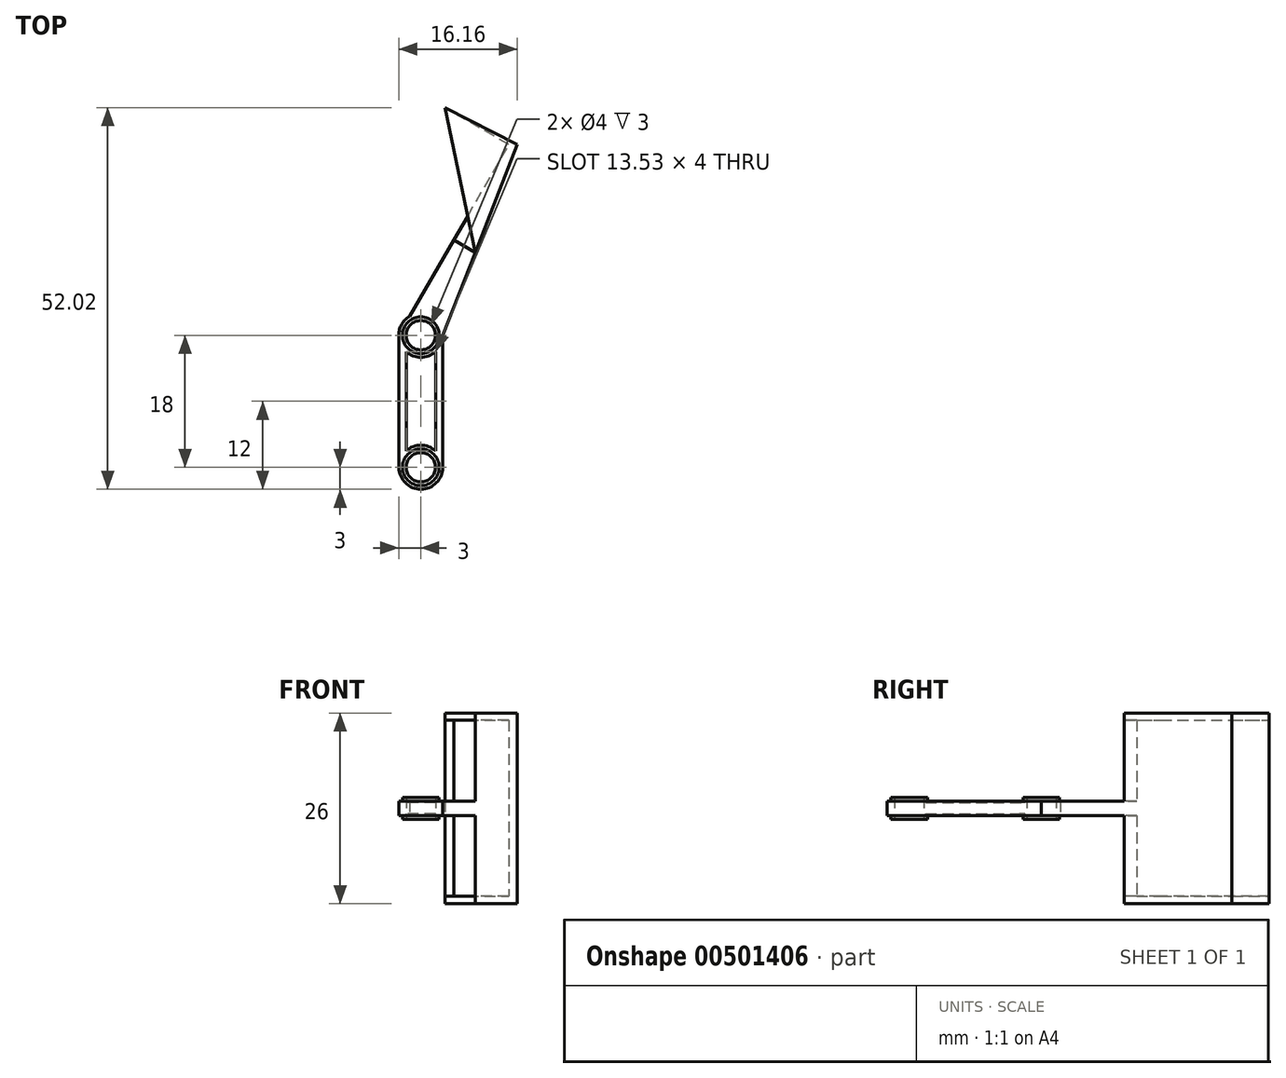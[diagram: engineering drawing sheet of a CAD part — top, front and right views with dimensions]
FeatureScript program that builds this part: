
annotation { "Feature Type Name" : "Feature", "Feature Type Description" : "" }
export const myFeature = defineFeature(function(context is Context, id is Id, definition is map)
    precondition{}
    {
        {
            var Q0;
            Q0=qCreatedBy(makeId("Front.planeOp"),FACE);
            var sketch = newSketch(context, id + "F0", { "sketchPlane" : qUnion([Q0])});
            skLineSegment(sketch, "E0.left", {"start": v(3, -1) * mm, "end": v(3, 1) * mm});
            skLineSegment(sketch, "E0.right", {"start": v(-3, -1) * mm, "end": v(-3, 1) * mm});
            skPoint(sketch, "E0.middle", {"position": v(0, 0) * mm});
            skLineSegment(sketch, "E1", {"start": v(-3, 1) * mm, "end": v(-2, 1) * mm});
            skLineSegment(sketch, "E2", {"start": v(-2, 1) * mm, "end": v(-2, 0.75) * mm});
            skLineSegment(sketch, "E3", {"start": v(-2, 0.75) * mm, "end": v(2, 0.75) * mm});
            skLineSegment(sketch, "E4", {"start": v(2, 0.75) * mm, "end": v(2, 1) * mm});
            skLineSegment(sketch, "E5", {"start": v(2, 1) * mm, "end": v(3, 1) * mm});
            skLineSegment(sketch, "E6", {"start": v(-3, -1) * mm, "end": v(-2, -1) * mm});
            skLineSegment(sketch, "E7", {"start": v(-2, -1) * mm, "end": v(-2, -0.75) * mm});
            skLineSegment(sketch, "E8", {"start": v(-2, -0.75) * mm, "end": v(2, -0.75) * mm});
            skLineSegment(sketch, "E9", {"start": v(2, -0.75) * mm, "end": v(2, -1) * mm});
            skLineSegment(sketch, "E10", {"start": v(2, -1) * mm, "end": v(3, -1) * mm});
            skSolve(sketch);
        }
        {
            var Q0;
            Q0=makeQuery(id+"F0.imprint","IMPRINT",FACE,{"disambiguationData":[TD([[makeQuery(id+"F0.imprint","IMPRINT",EDGE,{"derivedFrom":sQuery(id+"F0.wireOp",EDGE,"E0.left")}),1.0]])]});
            extrude(context, id + "F1", {"entities" : qUnion([Q0]), "endBound" : BoundingType.SYMMETRIC, "depth" : 18 * mm});
        }
        {
            var Q0;
            Q0=makeQuery(id+"F1.opExtrude","SWEPT_FACE",FACE,{"disambiguationData":[OSD([sQuery(id+"F0.wireOp",EDGE,"E8")])]});
            var sketch = newSketch(context, id + "F2", { "sketchPlane" : qUnion([Q0])});
            skCircle(sketch, "E11", {"center": v(0, 9) * mm, "radius": 2 * mm});
            skCircle(sketch, "E12", {"center": v(0, 9) * mm, "radius": 3 * mm});
            skCircle(sketch, "E13", {"center": v(0, -9) * mm, "radius": 2 * mm});
            skPoint(sketch, "E13.centerSnap0", {"position": v(0, -9) * mm});
            skCircle(sketch, "E14", {"center": v(0, -9) * mm, "radius": 3 * mm});
            skSolve(sketch);
        }
        {
            var Q0;
            {var subQ1=sQuery(id+"F0.wireOp",EDGE,"E8");var subQ2=makeQuery(id+"F1.opExtrude","CAP_EDGE",EDGE,{"disambiguationData":[OSD([subQ1])],"isStart":false});Q0=makeQuery(id+"F2.imprint","IMPRINT",FACE,{"disambiguationData":[TD([[makeQuery(id+"F2.imprint","IMPRINT",EDGE,{"derivedFrom":subQ2}),-1.0]])]});}
            extrude(context, id + "F3", {"entities" : qUnion([Q0]), "operationType" : NewBodyOperationType.REMOVE, "oppositeDirection" : true, "depth" : 2 * mm});
        }
        {
            var Q0;
            {var subQ1=sQuery(id+"F0.wireOp",EDGE,"E8");var subQ2=makeQuery(id+"F1.opExtrude","CAP_EDGE",EDGE,{"disambiguationData":[OSD([subQ1])],"isStart":true});Q0=makeQuery(id+"F2.imprint","IMPRINT",FACE,{"disambiguationData":[TD([[makeQuery(id+"F2.imprint","IMPRINT",EDGE,{"derivedFrom":subQ2}),1.0]])]});}
            extrude(context, id + "F4", {"entities" : qUnion([Q0]), "operationType" : NewBodyOperationType.REMOVE, "oppositeDirection" : true, "depth" : 2 * mm});
        }
        {
            var Q0;
            {var subQ1=sQuery(id+"F0.wireOp",EDGE,"E8");var subQ3=makeQuery(id+"F1.opExtrude","SWEPT_EDGE",EDGE,{"disambiguationData":[OSD([sQuery(id+"F0.wireOp",EDGE,"E7"),subQ1])]});var subQ7=sQuery(id+"F2.wireOp",EDGE,"E14");var subQ8=makeQuery(id+"F2.imprint","INTERSECT",VERTEX,{"derivedFrom":[subQ3,subQ7]});Q0=makeQuery(id+"F2.imprint","IMPRINT",FACE,{"disambiguationData":[TD([[makeQuery(id+"F2.imprint","IMPRINT",EDGE,{"disambiguationData":[TD([[subQ8,-1.0]])],"derivedFrom":subQ7}),1.0]])]});}
            var Q1;
            {var subQ1=sQuery(id+"F0.wireOp",EDGE,"E8");var subQ3=makeQuery(id+"F1.opExtrude","SWEPT_EDGE",EDGE,{"disambiguationData":[OSD([sQuery(id+"F0.wireOp",EDGE,"E7"),subQ1])]});var subQ7=sQuery(id+"F2.wireOp",EDGE,"E14");var subQ8=makeQuery(id+"F2.imprint","INTERSECT",VERTEX,{"derivedFrom":[subQ3,subQ7]});Q1=makeQuery(id+"F2.imprint","IMPRINT",FACE,{"disambiguationData":[TD([[makeQuery(id+"F2.imprint","IMPRINT",EDGE,{"disambiguationData":[TD([[subQ8,1.0]])],"derivedFrom":subQ7}),1.0]])]});}
            extrude(context, id + "F5", {"entities" : qUnion([Q0, Q1]), "operationType" : NewBodyOperationType.REMOVE, "oppositeDirection" : true, "depth" : 2 * mm});
        }
        {
            var Q0;
            {var subQ1=sQuery(id+"F0.wireOp",EDGE,"E8");var subQ3=makeQuery(id+"F1.opExtrude","SWEPT_EDGE",EDGE,{"disambiguationData":[OSD([sQuery(id+"F0.wireOp",EDGE,"E7"),subQ1])]});var subQ7=sQuery(id+"F2.wireOp",EDGE,"E14");var subQ8=makeQuery(id+"F2.imprint","INTERSECT",VERTEX,{"derivedFrom":[subQ3,subQ7]});Q0=makeQuery(id+"F2.imprint","IMPRINT",FACE,{"disambiguationData":[TD([[makeQuery(id+"F2.imprint","IMPRINT",EDGE,{"disambiguationData":[TD([[subQ8,-1.0]])],"derivedFrom":subQ7}),1.0]])]});}
            extrude(context, id + "F6", {"entities" : qUnion([Q0]), "operationType" : NewBodyOperationType.REMOVE, "oppositeDirection" : true, "depth" : 25 * mm});
        }
        {
            var Q0;
            {var subQ1=sQuery(id+"F0.wireOp",EDGE,"E8");var subQ3=makeQuery(id+"F1.opExtrude","SWEPT_EDGE",EDGE,{"disambiguationData":[OSD([sQuery(id+"F0.wireOp",EDGE,"E7"),subQ1])]});var subQ7=sQuery(id+"F2.wireOp",EDGE,"E14");var subQ8=makeQuery(id+"F2.imprint","INTERSECT",VERTEX,{"derivedFrom":[subQ3,subQ7]});Q0=makeQuery(id+"F2.imprint","IMPRINT",FACE,{"disambiguationData":[TD([[makeQuery(id+"F2.imprint","IMPRINT",EDGE,{"disambiguationData":[TD([[subQ8,-1.0]])],"derivedFrom":subQ7}),1.0]])]});}
            extrude(context, id + "F7", {"entities" : qUnion([Q0]), "operationType" : NewBodyOperationType.REMOVE, "oppositeDirection" : true, "depth" : 25 * mm});
        }
        {
            var Q0;
            {var subQ1=sQuery(id+"F0.wireOp",EDGE,"E8");var subQ3=makeQuery(id+"F1.opExtrude","SWEPT_EDGE",EDGE,{"disambiguationData":[OSD([sQuery(id+"F0.wireOp",EDGE,"E7"),subQ1])]});var subQ7=sQuery(id+"F2.wireOp",EDGE,"E14");var subQ8=makeQuery(id+"F2.imprint","INTERSECT",VERTEX,{"derivedFrom":[subQ3,subQ7]});Q0=makeQuery(id+"F2.imprint","IMPRINT",FACE,{"disambiguationData":[TD([[makeQuery(id+"F2.imprint","IMPRINT",EDGE,{"disambiguationData":[TD([[subQ8,-1.0]])],"derivedFrom":subQ7}),1.0]])]});}
            extrude(context, id + "F8", {"entities" : qUnion([Q0]), "operationType" : NewBodyOperationType.REMOVE, "oppositeDirection" : true, "depth" : 25 * mm});
        }
        {
            var Q0;
            {var subQ1=sQuery(id+"F0.wireOp",EDGE,"E8");var subQ3=makeQuery(id+"F1.opExtrude","SWEPT_EDGE",EDGE,{"disambiguationData":[OSD([sQuery(id+"F0.wireOp",EDGE,"E7"),subQ1])]});var subQ7=sQuery(id+"F2.wireOp",EDGE,"E14");var subQ8=makeQuery(id+"F2.imprint","INTERSECT",VERTEX,{"derivedFrom":[subQ3,subQ7]});Q0=makeQuery(id+"F2.imprint","IMPRINT",FACE,{"disambiguationData":[TD([[makeQuery(id+"F2.imprint","IMPRINT",EDGE,{"disambiguationData":[TD([[subQ8,-1.0]])],"derivedFrom":subQ7}),1.0]])]});}
            extrude(context, id + "F9", {"entities" : qUnion([Q0]), "operationType" : NewBodyOperationType.REMOVE, "depth" : 2 * mm});
        }
        {
            var Q0;
            {var subQ1=sQuery(id+"F0.wireOp",EDGE,"E8");var subQ3=makeQuery(id+"F1.opExtrude","SWEPT_EDGE",EDGE,{"disambiguationData":[OSD([sQuery(id+"F0.wireOp",EDGE,"E7"),subQ1])]});var subQ7=sQuery(id+"F2.wireOp",EDGE,"E12");var subQ8=makeQuery(id+"F2.imprint","INTERSECT",VERTEX,{"derivedFrom":[subQ3,subQ7]});Q0=makeQuery(id+"F2.imprint","IMPRINT",FACE,{"disambiguationData":[TD([[makeQuery(id+"F2.imprint","IMPRINT",EDGE,{"disambiguationData":[TD([[subQ8,1.0]])],"derivedFrom":subQ7}),1.0]])]});}
            var Q1;
            {var subQ1=sQuery(id+"F0.wireOp",EDGE,"E8");var subQ3=makeQuery(id+"F1.opExtrude","SWEPT_EDGE",EDGE,{"disambiguationData":[OSD([sQuery(id+"F0.wireOp",EDGE,"E7"),subQ1])]});var subQ7=sQuery(id+"F2.wireOp",EDGE,"E12");var subQ8=makeQuery(id+"F2.imprint","INTERSECT",VERTEX,{"derivedFrom":[subQ3,subQ7]});Q1=makeQuery(id+"F2.imprint","IMPRINT",FACE,{"disambiguationData":[TD([[makeQuery(id+"F2.imprint","IMPRINT",EDGE,{"disambiguationData":[TD([[subQ8,-1.0]])],"derivedFrom":subQ7}),1.0]])]});}
            extrude(context, id + "F10", {"entities" : qUnion([Q0, Q1]), "operationType" : NewBodyOperationType.REMOVE, "oppositeDirection" : true, "depth" : 2 * mm});
        }
        {
            var Q0;
            {var subQ1=sQuery(id+"F0.wireOp",EDGE,"E8");var subQ3=makeQuery(id+"F1.opExtrude","SWEPT_EDGE",EDGE,{"disambiguationData":[OSD([sQuery(id+"F0.wireOp",EDGE,"E7"),subQ1])]});var subQ7=sQuery(id+"F2.wireOp",EDGE,"E12");var subQ8=makeQuery(id+"F2.imprint","INTERSECT",VERTEX,{"derivedFrom":[subQ3,subQ7]});Q0=makeQuery(id+"F2.imprint","IMPRINT",FACE,{"disambiguationData":[TD([[makeQuery(id+"F2.imprint","IMPRINT",EDGE,{"disambiguationData":[TD([[subQ8,1.0]])],"derivedFrom":subQ7}),1.0]])]});}
            extrude(context, id + "F11", {"entities" : qUnion([Q0]), "operationType" : NewBodyOperationType.REMOVE, "depth" : 2 * mm});
        }
        {
            var Q0;
            {var subQ1=sQuery(id+"F0.wireOp",EDGE,"E8");var subQ3=makeQuery(id+"F1.opExtrude","SWEPT_EDGE",EDGE,{"disambiguationData":[OSD([sQuery(id+"F0.wireOp",EDGE,"E7"),subQ1])]});var subQ7=sQuery(id+"F2.wireOp",EDGE,"E14");var subQ8=makeQuery(id+"F2.imprint","INTERSECT",VERTEX,{"derivedFrom":[subQ3,subQ7]});Q0=makeQuery(id+"F2.imprint","IMPRINT",FACE,{"disambiguationData":[TD([[makeQuery(id+"F2.imprint","IMPRINT",EDGE,{"disambiguationData":[TD([[subQ8,1.0]])],"derivedFrom":subQ7}),1.0]])]});}
            var Q1;
            {var subQ1=sQuery(id+"F0.wireOp",EDGE,"E8");var subQ3=makeQuery(id+"F1.opExtrude","SWEPT_EDGE",EDGE,{"disambiguationData":[OSD([sQuery(id+"F0.wireOp",EDGE,"E7"),subQ1])]});var subQ7=sQuery(id+"F2.wireOp",EDGE,"E14");var subQ8=makeQuery(id+"F2.imprint","INTERSECT",VERTEX,{"derivedFrom":[subQ3,subQ7]});Q1=makeQuery(id+"F2.imprint","IMPRINT",FACE,{"disambiguationData":[TD([[makeQuery(id+"F2.imprint","IMPRINT",EDGE,{"disambiguationData":[TD([[subQ8,-1.0]])],"derivedFrom":subQ7}),1.0]])]});}
            var Q2;
            {var subQ1=sQuery(id+"F0.wireOp",EDGE,"E8");var subQ3=makeQuery(id+"F1.opExtrude","SWEPT_EDGE",EDGE,{"disambiguationData":[OSD([sQuery(id+"F0.wireOp",EDGE,"E7"),subQ1])]});var subQ7=sQuery(id+"F2.wireOp",EDGE,"E12");var subQ8=makeQuery(id+"F2.imprint","INTERSECT",VERTEX,{"derivedFrom":[subQ3,subQ7]});Q2=makeQuery(id+"F2.imprint","IMPRINT",FACE,{"disambiguationData":[TD([[makeQuery(id+"F2.imprint","IMPRINT",EDGE,{"disambiguationData":[TD([[subQ8,-1.0]])],"derivedFrom":subQ7}),1.0]])]});}
            var Q3;
            {var subQ1=sQuery(id+"F0.wireOp",EDGE,"E8");var subQ3=makeQuery(id+"F1.opExtrude","SWEPT_EDGE",EDGE,{"disambiguationData":[OSD([sQuery(id+"F0.wireOp",EDGE,"E7"),subQ1])]});var subQ7=sQuery(id+"F2.wireOp",EDGE,"E12");var subQ8=makeQuery(id+"F2.imprint","INTERSECT",VERTEX,{"derivedFrom":[subQ3,subQ7]});Q3=makeQuery(id+"F2.imprint","IMPRINT",FACE,{"disambiguationData":[TD([[makeQuery(id+"F2.imprint","IMPRINT",EDGE,{"disambiguationData":[TD([[subQ8,1.0]])],"derivedFrom":subQ7}),1.0]])]});}
            extrude(context, id + "F12", {"entities" : qUnion([Q0, Q1, Q2, Q3]), "operationType" : NewBodyOperationType.ADD, "oppositeDirection" : true, "depth" : 1.75 * mm});
        }
        {
            var Q0;
            {var subQ1=sQuery(id+"F0.wireOp",EDGE,"E8");var subQ3=makeQuery(id+"F1.opExtrude","SWEPT_EDGE",EDGE,{"disambiguationData":[OSD([sQuery(id+"F0.wireOp",EDGE,"E7"),subQ1])]});var subQ7=sQuery(id+"F2.wireOp",EDGE,"E14");var subQ8=makeQuery(id+"F2.imprint","INTERSECT",VERTEX,{"derivedFrom":[subQ3,subQ7]});Q0=makeQuery(id+"F2.imprint","IMPRINT",FACE,{"disambiguationData":[TD([[makeQuery(id+"F2.imprint","IMPRINT",EDGE,{"disambiguationData":[TD([[subQ8,1.0]])],"derivedFrom":subQ7}),1.0]])]});}
            var Q1;
            {var subQ1=sQuery(id+"F0.wireOp",EDGE,"E8");var subQ3=makeQuery(id+"F1.opExtrude","SWEPT_EDGE",EDGE,{"disambiguationData":[OSD([sQuery(id+"F0.wireOp",EDGE,"E7"),subQ1])]});var subQ7=sQuery(id+"F2.wireOp",EDGE,"E14");var subQ8=makeQuery(id+"F2.imprint","INTERSECT",VERTEX,{"derivedFrom":[subQ3,subQ7]});Q1=makeQuery(id+"F2.imprint","IMPRINT",FACE,{"disambiguationData":[TD([[makeQuery(id+"F2.imprint","IMPRINT",EDGE,{"disambiguationData":[TD([[subQ8,-1.0]])],"derivedFrom":subQ7}),1.0]])]});}
            var Q2;
            {var subQ1=sQuery(id+"F0.wireOp",EDGE,"E8");var subQ3=makeQuery(id+"F1.opExtrude","SWEPT_EDGE",EDGE,{"disambiguationData":[OSD([sQuery(id+"F0.wireOp",EDGE,"E7"),subQ1])]});var subQ7=sQuery(id+"F2.wireOp",EDGE,"E12");var subQ8=makeQuery(id+"F2.imprint","INTERSECT",VERTEX,{"derivedFrom":[subQ3,subQ7]});Q2=makeQuery(id+"F2.imprint","IMPRINT",FACE,{"disambiguationData":[TD([[makeQuery(id+"F2.imprint","IMPRINT",EDGE,{"disambiguationData":[TD([[subQ8,-1.0]])],"derivedFrom":subQ7}),1.0]])]});}
            var Q3;
            {var subQ1=sQuery(id+"F0.wireOp",EDGE,"E8");var subQ3=makeQuery(id+"F1.opExtrude","SWEPT_EDGE",EDGE,{"disambiguationData":[OSD([sQuery(id+"F0.wireOp",EDGE,"E7"),subQ1])]});var subQ7=sQuery(id+"F2.wireOp",EDGE,"E12");var subQ8=makeQuery(id+"F2.imprint","INTERSECT",VERTEX,{"derivedFrom":[subQ3,subQ7]});Q3=makeQuery(id+"F2.imprint","IMPRINT",FACE,{"disambiguationData":[TD([[makeQuery(id+"F2.imprint","IMPRINT",EDGE,{"disambiguationData":[TD([[subQ8,1.0]])],"derivedFrom":subQ7}),1.0]])]});}
            extrude(context, id + "F13", {"entities" : qUnion([Q0, Q1, Q2, Q3]), "operationType" : NewBodyOperationType.ADD, "depth" : .25 * mm});
        }
        {
            var Q0;
            Q0=makeQuery(id+"F13.boolean.opBoolean","MERGE",FACE,{"derivedFrom":[makeQuery(id+"F1.opExtrude","SWEPT_FACE",FACE,{"disambiguationData":[OSD([sQuery(id+"F0.wireOp",EDGE,"E6")])]}),makeQuery(id+"F1.opExtrude","SWEPT_FACE",FACE,{"disambiguationData":[OSD([sQuery(id+"F0.wireOp",EDGE,"E10")])]}),makeQuery(id+"F13.opExtrude","CAP_FACE",FACE,{"disambiguationData":[OSD([sQuery(id+"F2.wireOp",EDGE,"E11"),sQuery(id+"F2.wireOp",EDGE,"E12")])],"isStart":false}),makeQuery(id+"F13.opExtrude","CAP_FACE",FACE,{"disambiguationData":[OSD([sQuery(id+"F2.wireOp",EDGE,"E13"),sQuery(id+"F2.wireOp",EDGE,"E14")])],"isStart":false})]});
            var sketch = newSketch(context, id + "F14", { "sketchPlane" : qUnion([Q0])});
            skCircle(sketch, "E15", {"center": v(0, 9) * mm, "radius": 2 * mm});
            skCircle(sketch, "E16", {"center": v(0, 9) * mm, "radius": 2.5 * mm});
            skCircle(sketch, "E17", {"center": v(0, -9) * mm, "radius": 2 * mm});
            skCircle(sketch, "E18", {"center": v(0, -9) * mm, "radius": 2.5 * mm});
            skSolve(sketch);
        }
        {
            var Q0;
            Q0=makeQuery(id+"F14.imprint","IMPRINT",FACE,{"disambiguationData":[TD([[makeQuery(id+"F14.imprint","IMPRINT",EDGE,{"derivedFrom":sQuery(id+"F14.wireOp",EDGE,"E15")}),-1.0]])]});
            var Q1;
            Q1=makeQuery(id+"F14.imprint","IMPRINT",FACE,{"disambiguationData":[TD([[makeQuery(id+"F14.imprint","IMPRINT",EDGE,{"derivedFrom":sQuery(id+"F14.wireOp",EDGE,"E17")}),-1.0]])]});
            extrude(context, id + "F15", {"entities" : qUnion([Q0, Q1]), "operationType" : NewBodyOperationType.ADD, "depth" : .5 * mm});
        }
        {
            var Q0;
            Q0=makeQuery(id+"F12.boolean.opBoolean","MERGE",FACE,{"derivedFrom":[makeQuery(id+"F1.opExtrude","SWEPT_FACE",FACE,{"disambiguationData":[OSD([sQuery(id+"F0.wireOp",EDGE,"E1")])]}),makeQuery(id+"F1.opExtrude","SWEPT_FACE",FACE,{"disambiguationData":[OSD([sQuery(id+"F0.wireOp",EDGE,"E5")])]}),makeQuery(id+"F12.opExtrude","CAP_FACE",FACE,{"disambiguationData":[OSD([sQuery(id+"F2.wireOp",EDGE,"E11"),sQuery(id+"F2.wireOp",EDGE,"E12")])],"isStart":false}),makeQuery(id+"F12.opExtrude","CAP_FACE",FACE,{"disambiguationData":[OSD([sQuery(id+"F2.wireOp",EDGE,"E13"),sQuery(id+"F2.wireOp",EDGE,"E14")])],"isStart":false})]});
            var sketch = newSketch(context, id + "F16", { "sketchPlane" : qUnion([Q0])});
            skCircle(sketch, "E19", {"center": v(0, -9) * mm, "radius": 2 * mm});
            skCircle(sketch, "E20", {"center": v(0, -9) * mm, "radius": 2.5 * mm});
            skCircle(sketch, "E21", {"center": v(0, 9) * mm, "radius": 2 * mm});
            skCircle(sketch, "E22", {"center": v(0, 9) * mm, "radius": 2.5 * mm});
            skSolve(sketch);
        }
        {
            var Q0;
            Q0=makeQuery(id+"F16.imprint","IMPRINT",FACE,{"disambiguationData":[TD([[makeQuery(id+"F16.imprint","IMPRINT",EDGE,{"derivedFrom":sQuery(id+"F16.wireOp",EDGE,"E21")}),1.0]])]});
            var Q1;
            Q1=makeQuery(id+"F16.imprint","IMPRINT",FACE,{"disambiguationData":[TD([[makeQuery(id+"F16.imprint","IMPRINT",EDGE,{"derivedFrom":sQuery(id+"F16.wireOp",EDGE,"E19")}),1.0]])]});
            extrude(context, id + "F17", {"entities" : qUnion([Q0, Q1]), "operationType" : NewBodyOperationType.ADD, "depth" : .5 * mm});
        }
        {
            var Q0;
            Q0=qCreatedBy(makeId("Top.planeOp"),FACE);
            var sketch = newSketch(context, id + "F18", { "sketchPlane" : qUnion([Q0])});
            skLineSegment(sketch, "E23", {"start": v(0, 9) * mm, "end": v(-10.23, 14.9) * mm, "construction": true});
            skLineSegment(sketch, "E24", {"start": v(12, 34.98) * mm, "end": v(3.27, 40.02) * mm});
            skLineSegment(sketch, "E25", {"start": v(3.27, 40.02) * mm, "end": v(13.16, 34.98) * mm});
            skLineSegment(sketch, "E26", {"start": v(13.16, 34.98) * mm, "end": v(3, 9) * mm});
            skPoint(sketch, "E27", {"position": v(-3, 9) * mm});
            skPoint(sketch, "E28", {"position": v(-1.5, 11.6) * mm});
            skLineSegment(sketch, "E29.trimOffspring", {"start": v(-1.5, 11.6) * mm, "end": v(12, 34.98) * mm});
            skArc(sketch, "E30", {"start": v(3, 9) * mm, "mid": v(1.5, 11.6) * mm, "end": v(-1.5, 11.6) * mm});
            skPoint(sketch, "E31", {"position": v(4.5, 22) * mm});
            skLineSegment(sketch, "E32", {"start": v(4.5, 22) * mm, "end": v(7.42, 20.3) * mm});
            skSolve(sketch);
        }
        {
            var Q0;
            {var subQ0=sQuery(id+"F18.wireOp",EDGE,"E30");Q0=makeQuery(id+"F18.imprint","IMPRINT",FACE,{"disambiguationData":[TD([[makeQuery(id+"F18.imprint","IMPRINT",EDGE,{"derivedFrom":subQ0}),-1.0]])]});}
            extrude(context, id + "F19", {"entities" : qUnion([Q0]), "operationType" : NewBodyOperationType.ADD, "endBound" : BoundingType.SYMMETRIC, "depth" : 2 * mm});
        }
        {
            var Q0;
            {var subQ4=sQuery(id+"F18.wireOp",EDGE,"E24");Q0=makeQuery(id+"F18.imprint","IMPRINT",FACE,{"disambiguationData":[TD([[makeQuery(id+"F18.imprint","IMPRINT",EDGE,{"derivedFrom":subQ4}),-1.0]])]});}
            var Q1;
            Q1 = qSketchRegion(id + "F23", true);
            extrude(context, id + "F20", {"entities" : qUnion([Q0, Q1]), "operationType" : NewBodyOperationType.ADD, "endBound" : BoundingType.SYMMETRIC, "depth" : 24 * mm});
        }
        {
            var Q0;
            Q0=makeQuery(id+"F20.opExtrude","CAP_FACE",FACE,{"disambiguationData":[OSD([sQuery(id+"F18.wireOp",EDGE,"E24"),sQuery(id+"F18.wireOp",EDGE,"E25"),sQuery(id+"F18.wireOp",EDGE,"E26"),sQuery(id+"F18.wireOp",EDGE,"E29.trimOffspring"),sQuery(id+"F18.wireOp",EDGE,"E32")])],"isStart":true});
            var sketch = newSketch(context, id + "F21", { "sketchPlane" : qUnion([Q0])});
            skLineSegment(sketch, "E33", {"start": v(7.42, -20.3) * mm, "end": v(13.16, -34.98) * mm});
            skLineSegment(sketch, "E34", {"start": v(13.16, -34.98) * mm, "end": v(3.27, -40.02) * mm});
            skLineSegment(sketch, "E35", {"start": v(3.27, -40.02) * mm, "end": v(7.42, -20.3) * mm});
            skSolve(sketch);
        }
        {
            var Q0;
            Q0 = qSketchRegion(id + "F21", true);
            extrude(context, id + "F22", {"entities" : qUnion([Q0]), "operationType" : NewBodyOperationType.ADD, "depth" : 1 * mm});
        }
        {
            var Q0;
            Q0=makeQuery(id+"F20.opExtrude","CAP_FACE",FACE,{"disambiguationData":[OSD([sQuery(id+"F18.wireOp",EDGE,"E24"),sQuery(id+"F18.wireOp",EDGE,"E25"),sQuery(id+"F18.wireOp",EDGE,"E26"),sQuery(id+"F18.wireOp",EDGE,"E29.trimOffspring"),sQuery(id+"F18.wireOp",EDGE,"E32")])],"isStart":false});
            var sketch = newSketch(context, id + "F23", { "sketchPlane" : qUnion([Q0])});
            skLineSegment(sketch, "E36", {"start": v(7.42, 20.3) * mm, "end": v(3.27, 40.02) * mm});
            skLineSegment(sketch, "E37", {"start": v(3.27, 40.02) * mm, "end": v(13.16, 34.98) * mm});
            skLineSegment(sketch, "E38", {"start": v(13.16, 34.98) * mm, "end": v(7.42, 20.3) * mm});
            skSolve(sketch);
        }
        {
            var Q0;
            {var subQ1=makeQuery(id+"F20.opExtrude","CAP_EDGE",EDGE,{"disambiguationData":[OSD([sQuery(id+"F18.wireOp",EDGE,"E24")])],"isStart":false});Q0=makeQuery(id+"F23.imprint","IMPRINT",FACE,{"disambiguationData":[TD([[makeQuery(id+"F23.imprint","IMPRINT",EDGE,{"derivedFrom":subQ1}),1.0]])]});}
            var Q1;
            Q1=makeQuery(id+"F23.imprint","IMPRINT",FACE,{"disambiguationData":[TD([[makeQuery(id+"F23.imprint","IMPRINT",EDGE,{"derivedFrom":sQuery(id+"F23.wireOp",EDGE,"E37")}),-1.0]])]});
            extrude(context, id + "F24", {"entities" : qUnion([Q0, Q1]), "operationType" : NewBodyOperationType.ADD, "depth" : 1 * mm});
        }
    });
